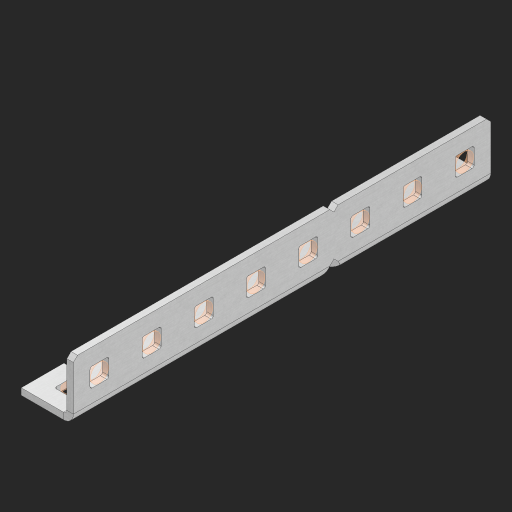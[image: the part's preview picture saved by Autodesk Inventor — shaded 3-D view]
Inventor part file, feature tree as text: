
AUTODESK INVENTOR PART (.ipt)
format: ipt  version: 2023 (Build 270158000, 158)  size: 670,720 bytes
history: native  units: in
note: dims shown in document units (in); Inventor stores cm internally (conversion verified against a paired STEP export)
features: other x172, extrude x22, sheet_metal_op x11, sketch x10, pattern_linear x2, mirror x1, chamfer x1
ambient origin geometry x8: Origin, YZ Plane, XZ Plane, XY Plane, X Axis, Y Axis, Z Axis, Center Point
bodies: Solid1 (feature_tree), Body (feature_tree)
feature tree (219):
  other  "Alu Half C 1x2x1x8"
  other  "Table"
  other  "Alu C 1x2x1x35"
  other  "Alu C 1x2x1x34"
  other  "Alu C 1x2x1x33"
  other  "Alu C 1x2x1x32"
  other  "Alu C 1x2x1x31"
  other  "Alu C 1x2x1x30"
  other  "Alu C 1x2x1x29"
  other  "Alu C 1x2x1x28"
  other  "Alu C 1x2x1x27"
  other  "Alu C 1x2x1x26"
  other  "Alu C 1x2x1x25"
  other  "Alu C 1x2x1x24"
  other  "Alu C 1x2x1x23"
  other  "Alu C 1x2x1x22"
  other  "Alu C 1x2x1x21"
  other  "Alu C 1x2x1x20"
  other  "Alu C 1x2x1x19"
  other  "Alu C 1x2x1x18"
  other  "Alu C 1x2x1x17"
  other  "Alu C 1x2x1x16"
  other  "Alu C 1x2x1x15"
  other  "Alu C 1x2x1x14"
  other  "Alu C 1x2x1x13"
  other  "Alu C 1x2x1x12"
  other  "Alu C 1x2x1x11"
  other  "Alu C 1x2x1x10"
  other  "Alu C 1x2x1x9"
  other  "Alu C 1x2x1x8"
  other  "Alu C 1x2x1x7"
  other  "Alu C 1x2x1x6"
  other  "Alu C 1x2x1x5"
  other  "Alu C 1x2x1x4"
  other  "Alu C 1x2x1x3"
  other  "Alu C 1x2x1x2"
  other  "Alu C 1x2x1x1"
  other  "Steel C 1x2x1x35"
  other  "Steel C 1x2x1x34"
  other  "Steel C 1x2x1x33"
  other  "Steel C 1x2x1x32"
  other  "Steel C 1x2x1x31"
  other  "Steel C 1x2x1x30"
  other  "Steel C 1x2x1x29"
  other  "Steel C 1x2x1x28"
  other  "Steel C 1x2x1x27"
  other  "Steel C 1x2x1x26"
  other  "Steel C 1x2x1x25"
  other  "Steel C 1x2x1x24"
  other  "Steel C 1x2x1x23"
  other  "Steel C 1x2x1x22"
  other  "Steel C 1x2x1x21"
  other  "Steel C 1x2x1x20"
  other  "Steel C 1x2x1x19"
  other  "Steel C 1x2x1x18"
  other  "Steel C 1x2x1x17"
  other  "Steel C 1x2x1x16"
  other  "Steel C 1x2x1x15"
  other  "Steel C 1x2x1x14"
  other  "Steel C 1x2x1x13"
  other  "Steel C 1x2x1x12"
  other  "Steel C 1x2x1x11"
  other  "Steel C 1x2x1x10"
  other  "Steel C 1x2x1x9"
  other  "Steel C 1x2x1x8"
  other  "Steel C 1x2x1x7"
  other  "Steel C 1x2x1x6"
  other  "Steel C 1x2x1x5"
  other  "Steel C 1x2x1x4"
  other  "Steel C 1x2x1x3"
  other  "Steel C 1x2x1x2"
  other  "Steel C 1x2x1x1"
  other  "Alu Half C 1x2x1x35"
  other  "Alu Half C 1x2x1x34"
  other  "Alu Half C 1x2x1x33"
  other  "Alu Half C 1x2x1x32"
  other  "Alu Half C 1x2x1x31"
  other  "Alu Half C 1x2x1x30"
  other  "Alu Half C 1x2x1x29"
  other  "Alu Half C 1x2x1x28"
  other  "Alu Half C 1x2x1x27"
  other  "Alu Half C 1x2x1x26"
  other  "Alu Half C 1x2x1x25"
  other  "Alu Half C 1x2x1x24"
  other  "Alu Half C 1x2x1x23"
  other  "Alu Half C 1x2x1x22"
  other  "Alu Half C 1x2x1x21"
  other  "Alu Half C 1x2x1x20"
  other  "Alu Half C 1x2x1x19"
  other  "Alu Half C 1x2x1x18"
  other  "Alu Half C 1x2x1x17"
  other  "Alu Half C 1x2x1x16"
  other  "Alu Half C 1x2x1x15"
  other  "Alu Half C 1x2x1x14"
  other  "Alu Half C 1x2x1x13"
  other  "Alu Half C 1x2x1x12"
  other  "Alu Half C 1x2x1x11"
  other  "Alu Half C 1x2x1x10"
  other  "Alu Half C 1x2x1x9"
  other  "Alu Half C 1x2x1x7"
  other  "Alu Half C 1x2x1x6"
  other  "Alu Half C 1x2x1x5"
  other  "Alu Half C 1x2x1x4"
  other  "Alu Half C 1x2x1x3"
  other  "Alu Half C 1x2x1x2"
  other  "Alu Half C 1x2x1x1"
  other  "Steel Half C 1x2x1x35"
  other  "Steel Half C 1x2x1x34"
  other  "Steel Half C 1x2x1x33"
  other  "Steel Half C 1x2x1x32"
  other  "Steel Half C 1x2x1x31"
  other  "Steel Half C 1x2x1x30"
  other  "Steel Half C 1x2x1x29"
  other  "Steel Half C 1x2x1x28"
  other  "Steel Half C 1x2x1x27"
  other  "Steel Half C 1x2x1x26"
  other  "Steel Half C 1x2x1x25"
  other  "Steel Half C 1x2x1x24"
  other  "Steel Half C 1x2x1x23"
  other  "Steel Half C 1x2x1x22"
  other  "Steel Half C 1x2x1x21"
  other  "Steel Half C 1x2x1x20"
  other  "Steel Half C 1x2x1x19"
  other  "Steel Half C 1x2x1x18"
  other  "Steel Half C 1x2x1x17"
  other  "Steel Half C 1x2x1x16"
  other  "Steel Half C 1x2x1x15"
  other  "Steel Half C 1x2x1x14"
  other  "Steel Half C 1x2x1x13"
  other  "Steel Half C 1x2x1x12"
  other  "Steel Half C 1x2x1x11"
  other  "Steel Half C 1x2x1x10"
  other  "Steel Half C 1x2x1x9"
  other  "Steel Half C 1x2x1x8"
  other  "Steel Half C 1x2x1x7"
  other  "Steel Half C 1x2x1x6"
  other  "Steel Half C 1x2x1x5"
  other  "Steel Half C 1x2x1x4"
  other  "Steel Half C 1x2x1x3"
  other  "Steel Half C 1x2x1x2"
  other  "Steel Half C 1x2x1x1"
  sheet_metal_op  "Flanges"
  other  "Flange Pattern Plane"
  other  "Flange Pattern Sketch"
  sheet_metal_op  "Flange Pattern"
  sheet_metal_op  "Body Pattern"
  pattern_linear  "Center Pattern"  Spacing1=0.0625in  [1 undecoded]
  other  "Arc Length"
  mirror  "Notch Mirror"
  pattern_linear  "Notch Pattern"  Spacing1=0.182in  [1 undecoded]
  chamfer  "End Chamfer"
  extrude  "Half Cut"  Depth=0.02in
  sketch  "Sketch1"  dims[d0=1.0in]
  other  "Plate1"
  sketch  "Sketch2"  dims[d1=4.0in]
  other  "Plate2"
  sheet_metal_op  "Bend1"
  sheet_metal_op  "Corner1"
  sketch  "Sketch3"  dims[d2=0.0625in]
  sketch  "Sketch7"  dims[d3=0.0625in]
  other  "Srf1"
  other  "Srf2"
  sketch  "Sketch8"  dims[d4=0.0312in]
  sketch  "Sketch9"  dims[d5=0.125in]
  other  "Srf91"
  sheet_metal_op  "Body Pattern Sketch"
  other  "Srf92"
  sketch  "Sketch13"  dims[d6=0.0625in]
  sketch  "Sketch14"  dims[d7=0.5in d8=90.0deg d9=0.0312in]
  sketch  "Sketch15"  dims[d10=0.25in]
  sketch  "Sketch16"  dims[d11=0.0625in d12=0.0625in d16=0.182in d17=0.02in d18=0.0625in d19=0.0in d20=0.25in d21=0.25in d38=3.1496in d40=0.5in d41=0.3937in d43=1.0in d46=0.172in d47=1.0in d48=0.0in d49=0.182in d50=0.02in d51=0.25in d52=0.25in d53=0.0625in d54=0.0in d55=0.172in d56=1.0in d57=0.0in d58=0.25in d60=3.1496in d62=0.5in d63=0.3937in d65=0.5in d85=0.1473in d86=0.1782in d88=0.04in d89=0.0625in d90=0.0in d91=0.04in d92=0.0491in d95=2.5in d96=0.04in d97=0.25in d98=45.0deg d99=0.25in d100=0.5in d101=0.0in d102=2.497in d106=0.182in d107=0.02in d108=0.5in d109=0.5in d110=0.0625in d111=0.0in d112=0.172in d113=0.5in d114=0.0in d117=0.5in d118=0.5in d119=0.5in]
  other  "Srf786"
  other  "Srf823"
  other  "Srf824"
  other  "Srf825"
  other  "Srf826"
  other  "Srf827"
  other  "Srf828"
  other  "Srf856"
  other  "Srf857"
  other  "Srf858"
  other  "Srf859"
  other  "Srf860"
  other  "Srf861"
  other  "Srf889"
  other  "Srf890"
  other  "Srf891"
  other  "Srf892"
  other  "Srf893"
  other  "Srf894"
  other  "Srf895"
  sheet_metal_op  "Flange Stamp"
  sheet_metal_op  "Flange Circle"
  sheet_metal_op  "Body Stamp"
  sheet_metal_op  "Body Circle"
  other  "Center Stamp"
  other  "Center Circle"
  sheet_metal_op  "Notch"
  extrude  "ExtrusionSrf2"  Depth=0.0625in
  extrude  "ExtrusionSrf92"  TaperAngle=0.0deg  [1 undecoded]
  extrude  "ExtrusionSrf823"  Depth=0.25in
  extrude  "ExtrusionSrf824"  Depth=0.25in
  extrude  "ExtrusionSrf825"  Depth=0.5in
  extrude  "ExtrusionSrf826"  Depth=0.5in
  extrude  "ExtrusionSrf827"  Depth=1.0in TaperAngle=0.0deg
  extrude  "ExtrusionSrf828"  Depth=0.182in
  extrude  "ExtrusionSrf856"  Depth=0.02in
  extrude  "ExtrusionSrf857"  Depth=0.25in
  extrude  "ExtrusionSrf858"  Depth=0.25in
  extrude  "ExtrusionSrf859"  Depth=0.0625in
  extrude  "ExtrusionSrf860"  TaperAngle=0.0deg  [1 undecoded]
  extrude  "ExtrusionSrf861"  Depth=0.5in
  extrude  "ExtrusionSrf889"  Depth=1.0in TaperAngle=0.0deg
  extrude  "ExtrusionSrf890"  Depth=0.25in
  extrude  "ExtrusionSrf891"  Depth=0.5in
  extrude  "ExtrusionSrf892"  Depth=0.5in
  extrude  "ExtrusionSrf893"  Depth=0.5in
  extrude  "ExtrusionSrf894"  Depth=0.5in
  extrude  "ExtrusionSrf895"  Depth=0.5in
note: 4 required parameter values undecoded (feature->parameter linkage not recoverable at this tier; creation-order binding heuristic only, values carry confidence <= 0.55)
